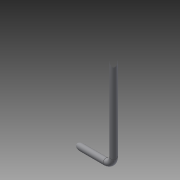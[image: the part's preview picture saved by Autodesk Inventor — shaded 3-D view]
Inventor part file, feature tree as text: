
AUTODESK INVENTOR PART (.ipt)
format: ipt  version: 2014 SP1 (Build 180222100, 222)  size: 75,264 bytes
history: native  units: in
note: dims shown in document units (in); Inventor stores cm internally (conversion verified against a paired STEP export)
features: other x3, sketch x2
ambient origin geometry x8: Origin, YZ Plane, XZ Plane, XY Plane, X Axis, Y Axis, Z Axis, Center Point
bodies: Solid1 (feature_tree)
feature tree (5):
  other  "Wheel Bar.ipt"
  other  "Solid1::Wheel Bar.ipt"
  other  "TaggingFeature1"
  sketch  "Sketch1"  dims[d0=0.3937in]
  sketch  "Sketch2"  dims[d3=0.3in d4=0.0in d5=5.5in d6=0.375in]
